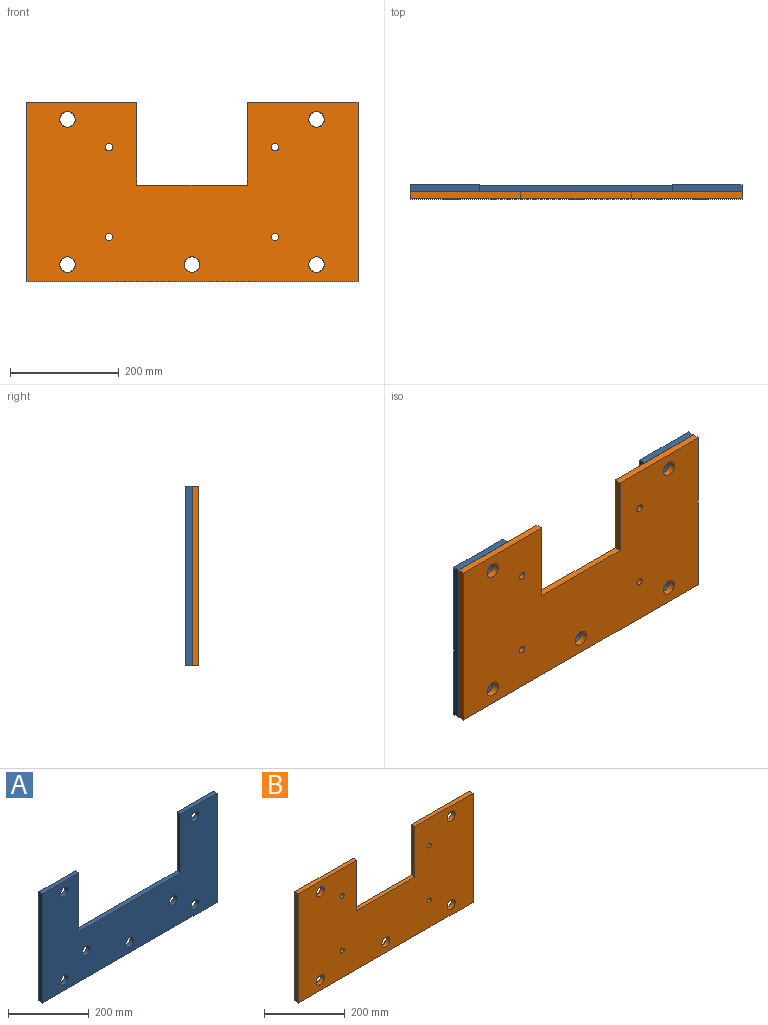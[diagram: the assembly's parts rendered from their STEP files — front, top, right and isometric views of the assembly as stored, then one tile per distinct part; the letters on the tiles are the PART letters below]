
ASSEMBLY  parts=2 mates=1
PART A: 17 faces, bbox 609.6x12.7x330.2 mm
  f0: plane 330.2x12.7mm, normal (-1,0,0), area 4193.5mm2, adj f1,f7,f8,f9
  f1: plane 609.6x12.7mm, normal (0,0,-1), area 7741.9mm2, adj f0,f2,f8,f9
  f2: plane 330.2x12.7mm, normal (1,0,0), area 4193.5mm2, adj f1,f3,f8,f9
  f3: plane 127x12.7mm, normal (0,0,1), area 1612.9mm2, adj f2,f4,f8,f9
  f4: plane 177.8x12.7mm, normal (-1,0,0), area 2258.1mm2, adj f3,f5,f8,f9
  f5: plane 355.6x12.7mm, normal (0,0,1), area 4516.1mm2, adj f4,f6,f8,f9
  f6: plane 177.8x12.7mm, normal (1,0,0), area 2258.1mm2, adj f5,f7,f8,f9
  f7: plane 127x12.7mm, normal (0,0,1), area 1612.9mm2, adj f0,f6,f8,f9
  f8: plane 609.6x330.2mm, normal (0,-1,0), area 133575.1mm2, adj f0,f1,f2,f3,f4,f5,f6,f7
  f9: plane 609.6x330.2mm, normal (0,1,0), area 133575.1mm2, adj f0,f1,f2,f3,f4,f5,f6,f7
  f10: cylinder r=14.29mm len=28.58mm, axis (0,1,0), area 1140.1mm2, adj f8,f9
  f11: cylinder r=14.29mm len=28.58mm, axis (0,1,0), area 1140.1mm2, adj f8,f9
  f12: cylinder r=14.29mm len=28.58mm, axis (0,1,0), area 1140.1mm2, adj f8,f9
  f13: cylinder r=14.29mm len=28.58mm, axis (0,1,0), area 1140.1mm2, adj f8,f9
  f14: cylinder r=14.29mm len=28.58mm, axis (0,1,0), area 1140.1mm2, adj f8,f9
  f15: cylinder r=14.29mm len=28.58mm, axis (0,1,0), area 1140.1mm2, adj f8,f9
  f16: cylinder r=14.29mm len=28.58mm, axis (0,1,0), area 1140.1mm2, adj f8,f9
PART B: 19 faces, bbox 609.6x12.7x330.2 mm
  f0: plane 152.4x12.7mm, normal (1,0,0), area 1935.5mm2, adj f1,f7,f8,f9
  f1: plane 203.2x12.7mm, normal (0,0,1), area 2580.6mm2, adj f0,f2,f8,f9
  f2: plane 330.2x12.7mm, normal (-1,0,0), area 4193.5mm2, adj f1,f3,f8,f9
  f3: plane 609.6x12.7mm, normal (0,0,-1), area 7741.9mm2, adj f2,f4,f8,f9
  f4: plane 330.2x12.7mm, normal (1,0,0), area 4193.5mm2, adj f3,f5,f8,f9
  f5: plane 203.2x12.7mm, normal (0,0,1), area 2580.6mm2, adj f4,f6,f8,f9
  f6: plane 152.4x12.7mm, normal (-1,0,0), area 1935.5mm2, adj f5,f7,f8,f9
  f7: plane 203.2x12.7mm, normal (0,0,1), area 2580.6mm2, adj f0,f6,f8,f9
  f8: plane 609.6x330.2mm, normal (0,-1,0), area 166543.2mm2, adj f0,f1,f2,f3,f4,f5,f6,f7
  f9: plane 609.6x330.2mm, normal (0,1,0), area 166543.2mm2, adj f0,f1,f2,f3,f4,f5,f6,f7
  f10: cylinder r=14.29mm len=28.58mm, axis (0,-1,0), area 1140.1mm2, adj f8,f9
  f11: cylinder r=14.29mm len=28.58mm, axis (0,-1,0), area 1140.1mm2, adj f8,f9
  f12: cylinder r=14.29mm len=28.58mm, axis (0,-1,0), area 1140.1mm2, adj f8,f9
  f13: cylinder r=14.29mm len=28.58mm, axis (0,-1,0), area 1140.1mm2, adj f8,f9
  f14: cylinder r=14.29mm len=28.58mm, axis (0,-1,0), area 1140.1mm2, adj f8,f9
  f15: cylinder r=6.75mm len=13.5mm, axis (0,-1,0), area 538.6mm2, adj f8,f9
  f16: cylinder r=6.75mm len=13.5mm, axis (0,-1,0), area 538.6mm2, adj f8,f9
  f17: cylinder r=6.75mm len=13.5mm, axis (0,-1,0), area 538.6mm2, adj f8,f9
  f18: cylinder r=6.75mm len=13.5mm, axis (0,-1,0), area 538.6mm2, adj f8,f9
PLACE A rot(axis=(0,0,1),180deg) t=(0,0,16.02)mm
PLACE B t=(0,-6.35,16.02)mm
MATE fastened A.f9 <-> B.f9  axis (0,-1,0) through (304.8,0,181.12)mm
